# Revit family: WicStyle65evo_Single_leaf_Double_action_door
name_source: partatom
category: Doors
revit_build: Autodesk Revit Architecture 2014 (Build: 20130308_1515(x64)
units: mm (PartAtom-declared; Revit-internal decimal feet)

## types (1)
- WicStyle65evo_Single_leaf_Double_action_door
    Acoustic = RA,tr = 35 dB
    Air Permeability = Class 4
    Analytic Construction = <None>
    Corrosion Resistance of the Fittings = NPD
    Date of publishing = 3/14/2015
    Description = Wicslide 65 sliding windows and patio doors is the perfect solution for combining high thermal performance and large sizes. With  its  various  designs  of  outer  and  opening  frames, multiple  leaf  combinations  (from  2  to  6  leaves)  and  its  comprehensive range of dual colour solutions, the Wicslide 65 brings greater freedom to building design. Designed  to  meet  market  demands,  Wicslide  65  sliding doors are perfectly suited for disabled access.
    Design country = Germany
    Door Offset = 60 mm  [stored 0.19685 ft]
    EN1627 Burglar Resistance = NPD
    Edition number = 1
    Frame 1926541 = Yes
    Frame 1926542 = No
    Frame Thickness = 65 mm  [stored 0.213255 ft]
    Frame Width = 37 mm
    Frame Width 2 = 26 mm
    Frame Width 3 = 43 mm
    FrameWarning = 1
    Function = Interior
    Glass Material = WICONA -  Glass
    Height = 2200 mm
    Keynote = L10/330
    Leaf Height = 2088 mm  [stored 6.85039 ft]
    Leaf Width = 674 mm
    Load Bearing Capacity of Safety Devices = Fulfilled
    Manufacturer = Wicona
    Manufacturer country = Germany
    Manufacturer name = Wicona
    Material main = Aluminium
    Material secondary = Glass
    Maximum Sash Weight = 150kg as standard design, heavier weights can easily be customised
    Mechanical Strength = Class 4
    Model = Wicslide 65 evo
    Nominal height = 210000
    Nominal width = 150000
    Opening Line Length = 714 mm
    Operating Forces = Class 1
    Operation = IFC_DOORDBLSWING
    Product Guid = 1ef816c7-8b64-491b-b226-0f81c5fb437c
    Product SKU = WICSTYLE_65_EVO_D
    Product data url = http://bimobject.com
    Product family = Windows & Doors
    Product group = Windows
    QR code = http://bimobject.com
    Quality Assurance = Certified according to ISO 9001:2008
    Repeated Opening/Closing = Class 2 (10,000 Cycles)
    Sash Profil 1926540 Pivot 3926505 = Yes
    Sash Profil 1926540 Pivot 4930098 = No
    SashWarning = 1
    Threshold Height = 19 mm
    Threshold Length = 714 mm
    URL = http://www.wicona.com
    Uniclass2 = Ss-25-30-95-28
    Wall Closure = By host
    WarningSign = No
    Watertightness = E900
    Weight Net (Kg) = 0
    Width = 800 mm  [stored 2.62467 ft]

note: [stored X ft] marks values corroborated as IEEE doubles in the binary element streams (Revit-internal decimal feet)

## geometry (parser evidence)
native form markers: Blend x4, Sweep x10
no freeform markers — native parametric forms only
